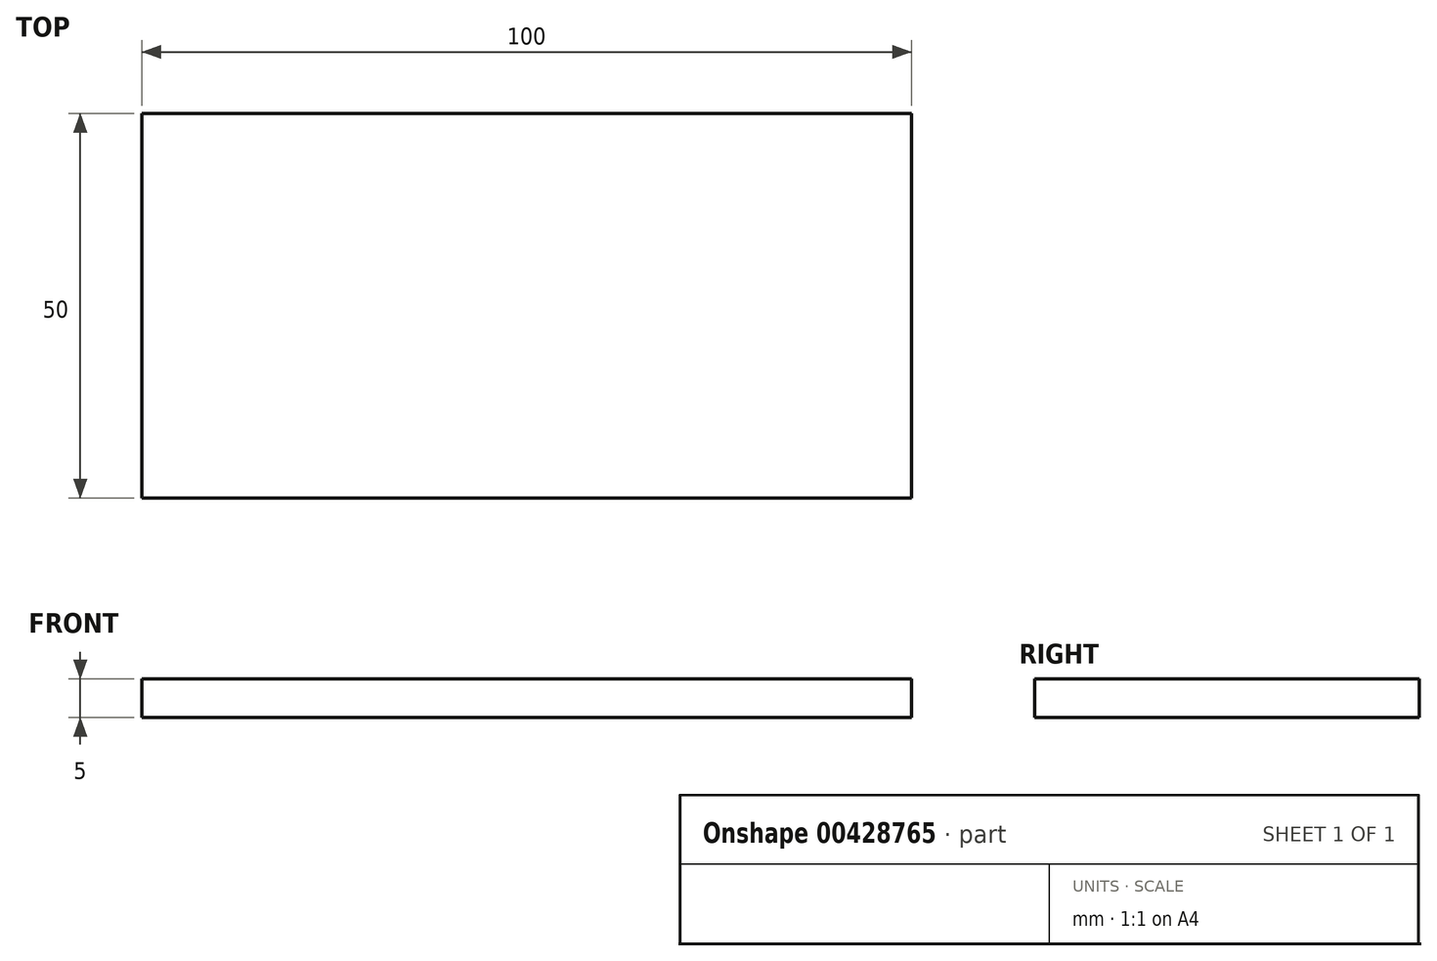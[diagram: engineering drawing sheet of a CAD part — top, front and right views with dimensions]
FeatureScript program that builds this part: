
annotation { "Feature Type Name" : "Feature", "Feature Type Description" : "" }
export const myFeature = defineFeature(function(context is Context, id is Id, definition is map)
    precondition{}
    {
        {
            var Q0;
            Q0=qCreatedBy(makeId("Top.planeOp"),FACE);
            var sketch = newSketch(context, id + "F0", { "sketchPlane" : qUnion([Q0])});
            skLineSegment(sketch, "E0.bottom", {"start": v(-59.64, 20) * mm, "end": v(40.36, 20) * mm});
            skLineSegment(sketch, "E0.top", {"start": v(-59.64, -30) * mm, "end": v(40.36, -30) * mm});
            skLineSegment(sketch, "E0.left", {"start": v(-59.64, 20) * mm, "end": v(-59.64, -30) * mm});
            skLineSegment(sketch, "E0.right", {"start": v(40.36, 20) * mm, "end": v(40.36, -30) * mm});
            skSolve(sketch);
        }
        {
            var Q0;
            Q0 = qSketchRegion(id + "F0", true);
            extrude(context, id + "F1", {"entities" : qUnion([Q0]), "depth" : 5 * mm});
        }
    });
